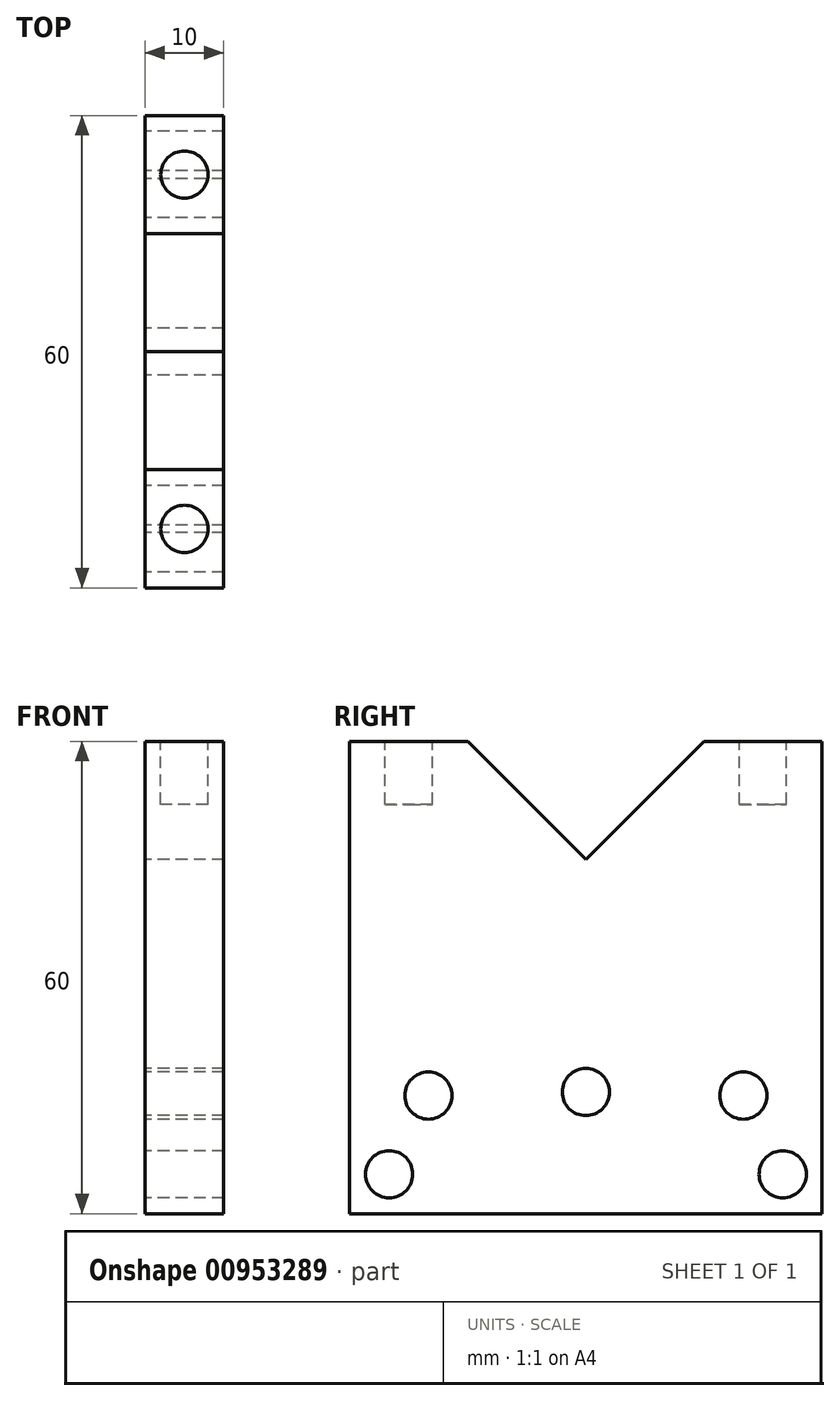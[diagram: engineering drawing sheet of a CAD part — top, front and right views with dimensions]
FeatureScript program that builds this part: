
annotation { "Feature Type Name" : "Feature", "Feature Type Description" : "" }
export const myFeature = defineFeature(function(context is Context, id is Id, definition is map)
    precondition{}
    {
        {
            var Q0;
            Q0=qCreatedBy(makeId("Right.planeOp"),FACE);
            var sketch = newSketch(context, id + "F0", { "sketchPlane" : qUnion([Q0])});
            skLineSegment(sketch, "E0.top", {"start": v(-30, -4.92) * mm, "end": v(30, -4.92) * mm});
            skLineSegment(sketch, "E0.left", {"start": v(-30, 55.08) * mm, "end": v(-30, -4.92) * mm});
            skLineSegment(sketch, "E0.right", {"start": v(30, 55.08) * mm, "end": v(30, -4.92) * mm});
            skLineSegment(sketch, "E1", {"start": v(-30, 55.08) * mm, "end": v(-15, 55.08) * mm});
            skLineSegment(sketch, "E2", {"start": v(15, 55.08) * mm, "end": v(30, 55.08) * mm});
            skLineSegment(sketch, "E3", {"start": v(-15, 55.08) * mm, "end": v(0, 40.08) * mm});
            skLineSegment(sketch, "E4", {"start": v(0, 40.08) * mm, "end": v(15, 55.08) * mm});
            skCircle(sketch, "E5", {"center": v(-20, 10.08) * mm, "radius": 3 * mm});
            skCircle(sketch, "E6", {"center": v(20, 10.08) * mm, "radius": 3 * mm});
            skCircle(sketch, "E7", {"center": v(0, 10.54) * mm, "radius": 3 * mm});
            skCircle(sketch, "E8", {"center": v(-25, 0.08) * mm, "radius": 3 * mm});
            skCircle(sketch, "E9", {"center": v(25, 0.08) * mm, "radius": 3 * mm});
            skSolve(sketch);
        }
        {
            var Q0;
            Q0 = qSketchRegion(id + "F0", true);
            extrude(context, id + "F1", {"entities" : qUnion([Q0]), "depth" : 10 * mm, "offsetDistance" : 25 * mm});
        }
        {
            var Q0;
            Q0=makeQuery(id+"F1.opExtrude","SWEPT_FACE",FACE,{"disambiguationData":[OSD([sQuery(id+"F0.wireOp",EDGE,"E2")])]});
            var sketch = newSketch(context, id + "F2", { "sketchPlane" : qUnion([Q0])});
            skCircle(sketch, "E10", {"center": v(5, 22.5) * mm, "radius": 3 * mm});
            skPoint(sketch, "E10.centerSnap0", {"position": v(10, 22.5) * mm});
            skPoint(sketch, "E10.centerSnap1", {"position": v(5, 30) * mm});
            skSolve(sketch);
        }
        {
            var Q0;
            Q0=makeQuery(id+"F1.opExtrude","SWEPT_FACE",FACE,{"disambiguationData":[OSD([sQuery(id+"F0.wireOp",EDGE,"E1")])]});
            var sketch = newSketch(context, id + "F3", { "sketchPlane" : qUnion([Q0])});
            skCircle(sketch, "E11", {"center": v(5, -22.5) * mm, "radius": 3 * mm});
            skPoint(sketch, "E11.centerSnap0", {"position": v(10, -22.5) * mm});
            skPoint(sketch, "E11.centerSnap1", {"position": v(5, -15) * mm});
            skSolve(sketch);
        }
        {
            var Q0;
            Q0 = qSketchRegion(id + "F2", true);
            var Q1;
            Q1 = qSketchRegion(id + "F3", true);
            extrude(context, id + "F4", {"entities" : qUnion([Q0, Q1]), "operationType" : NewBodyOperationType.REMOVE, "oppositeDirection" : true, "depth" : 8 * mm, "offsetDistance" : 25 * mm});
        }
    });
